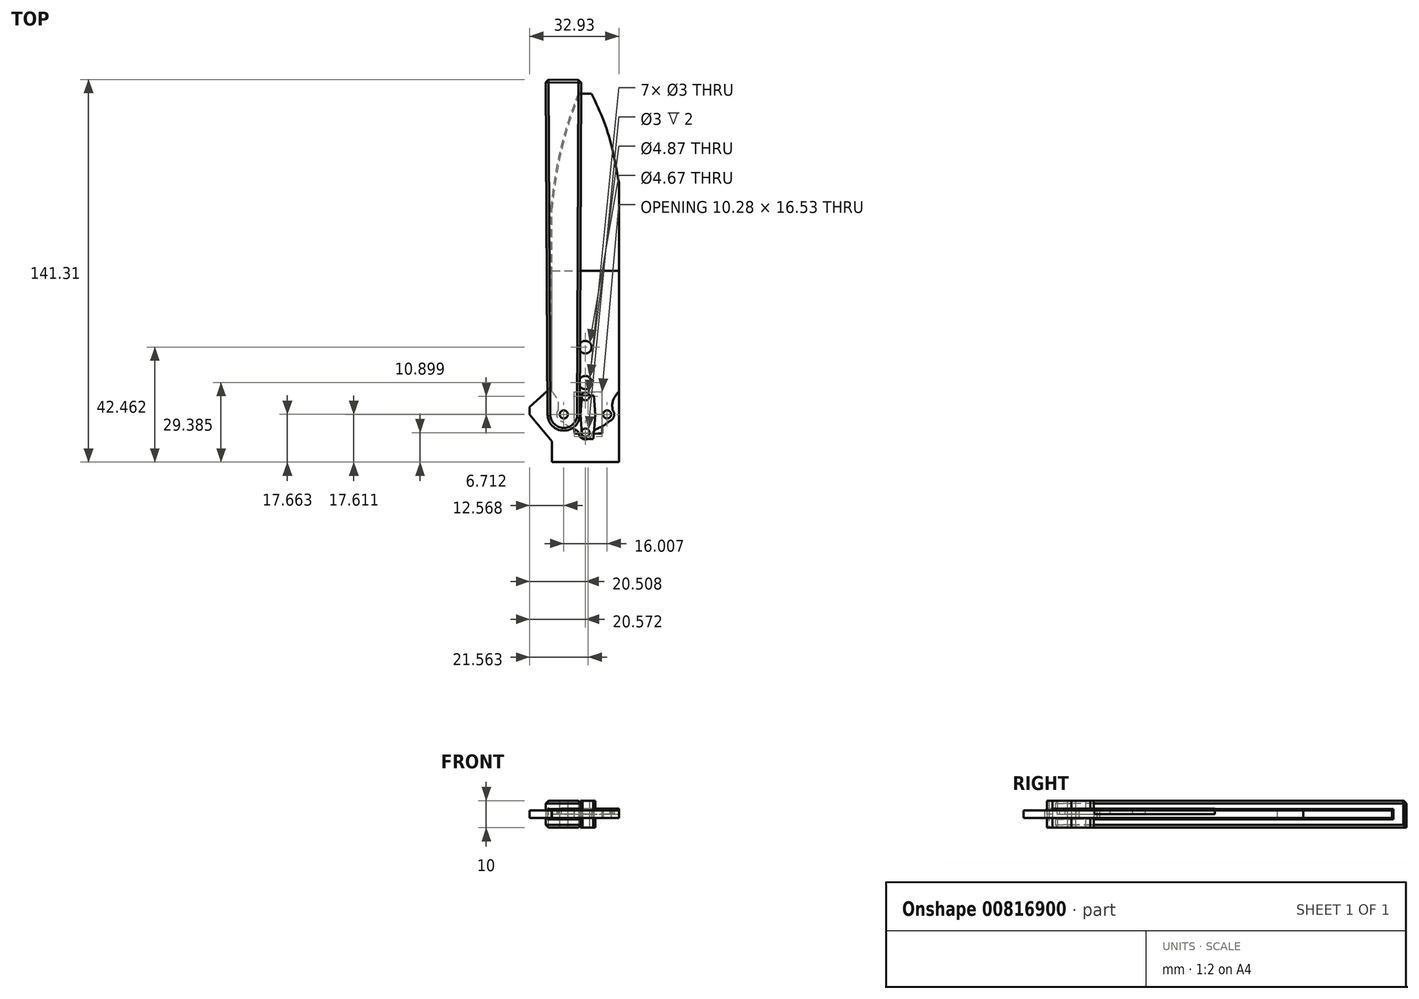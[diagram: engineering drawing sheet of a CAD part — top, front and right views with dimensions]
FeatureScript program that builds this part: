
annotation { "Feature Type Name" : "Feature", "Feature Type Description" : "" }
export const myFeature = defineFeature(function(context is Context, id is Id, definition is map)
    precondition{}
    {
        {
            var Q0;
            Q0=qCreatedBy(makeId("Top.planeOp"),FACE);
            var sketch = newSketch(context, id + "F0", { "sketchPlane" : qUnion([Q0])});
            skLineSegment(sketch, "E0.bottom", {"start": v(-13.28, -70.6) * mm, "end": v(11.44, -70.6) * mm});
            skLineSegment(sketch, "E0.top", {"start": v(-13.28, 65.4) * mm, "end": v(11.44, 65.4) * mm});
            skLineSegment(sketch, "E0.left", {"start": v(-13.28, -70.6) * mm, "end": v(-13.28, 22.93) * mm});
            skLineSegment(sketch, "E0.right", {"start": v(11.44, -70.6) * mm, "end": v(11.44, 32.61) * mm});
            skLineSegment(sketch, "E1", {"start": v(-0.92, 65.4) * mm, "end": v(-0.92, -70.6) * mm, "construction": true});
            skCircle(sketch, "E2", {"center": v(-0.92, -59.71) * mm, "radius": 1.5 * mm});
            skCircle(sketch, "E3", {"center": v(-0.92, -46.29) * mm, "radius": 1.5 * mm});
            skLineSegment(sketch, "E4", {"start": v(-13.28, -53) * mm, "end": v(-0.92, -53) * mm, "construction": true});
            skCircle(sketch, "E5", {"center": v(-8.92, -53) * mm, "radius": 1.5 * mm});
            skCircle(sketch, "E6.MirrorC", {"center": v(7.08, -53) * mm, "radius": 1.5 * mm});
            skFitSpline(sketch, "E7", {"points": [v(-3.02, 65.4) * mm, v(-6.8, 55.16) * mm, v(-11.04, 38.52) * mm, v(-13.28, 22.93) * mm], "startDerivative": vector(-13.1, -32.8) * mm, "endDerivative": vector(-5.15, -43.8) * mm});
            skFitSpline(sketch, "E8", {"points": [v(1.36, 65.4) * mm, v(7.27, 51.38) * mm, v(11.44, 32.61) * mm], "startDerivative": vector(13.66, -28.43) * mm, "endDerivative": vector(6.64, -36.96) * mm});
            skLineSegment(sketch, "E9", {"start": v(-13.28, -42.85) * mm, "end": v(-21.49, -50.18) * mm});
            skLineSegment(sketch, "E10", {"start": v(-21.49, -50.18) * mm, "end": v(-21.49, -53) * mm});
            skLineSegment(sketch, "E11", {"start": v(-21.49, -53) * mm, "end": v(-13.28, -62.88) * mm});
            skSolve(sketch);
        }
        {
            var Q0;
            Q0=makeQuery(id+"F0.imprint","IMPRINT",FACE,{"disambiguationData":[TD([[makeQuery(id+"F0.imprint","IMPRINT",EDGE,{"derivedFrom":sQuery(id+"F0.wireOp",EDGE,"E0.bottom")}),1.0]])]});
            var Q1;
            {var subQ0=sQuery(id+"F0.wireOp",EDGE,"E9");Q1=makeQuery(id+"F0.imprint","IMPRINT",FACE,{"disambiguationData":[TD([[makeQuery(id+"F0.imprint","IMPRINT",EDGE,{"derivedFrom":subQ0}),1.0]])]});}
            extrude(context, id + "F1", {"entities" : qUnion([Q0, Q1]), "endBound" : BoundingType.SYMMETRIC, "depth" : 2.75 * mm, "offsetDistance" : 25 * mm});
        }
        {
            var Q0;
            Q0=qCreatedBy(makeId("Top.planeOp"),FACE);
            var sketch = newSketch(context, id + "F2", { "sketchPlane" : qUnion([Q0])});
            skCircle(sketch, "E12.0", {"center": v(-8.92, -53) * mm, "radius": 1.5 * mm});
            skCircle(sketch, "E13.0", {"center": v(-0.92, -46.29) * mm, "radius": 1.5 * mm});
            skCircle(sketch, "E14.0", {"center": v(-0.92, -59.71) * mm, "radius": 1.5 * mm});
            skArc(sketch, "E15", {"start": v(-14.89, -53.03) * mm, "mid": v(-8.92, -58.97) * mm, "end": v(-2.95, -53.02) * mm});
            skLineSegment(sketch, "E16", {"start": v(-2.54, 70.47) * mm, "end": v(-15.54, 70.72) * mm});
            skLineSegment(sketch, "E17", {"start": v(-15.54, 70.72) * mm, "end": v(-14.89, -53.03) * mm});
            skLineSegment(sketch, "E18", {"start": v(-2.54, 70.47) * mm, "end": v(-2.95, -53.02) * mm});
            skPoint(sketch, "E19.centerSnap0", {"position": v(-9.04, 70.6) * mm});
            skSolve(sketch);
        }
        {
            var Q0;
            Q0 = qSketchRegion(id + "F2", true);
            extrude(context, id + "F3", {"entities" : qUnion([Q0]), "endBound" : BoundingType.SYMMETRIC, "depth" : 10 * mm, "offsetDistance" : 25 * mm});
        }
        {
            var Q0;
            Q0=makeQuery(id+"F1.opExtrude","SWEPT_BODY",BODY,{"disambiguationData":[OSD([sQuery(id+"F0.wireOp",EDGE,"E0.bottom"),sQuery(id+"F0.wireOp",EDGE,"E0.top"),sQuery(id+"F0.wireOp",EDGE,"E0.left"),sQuery(id+"F0.wireOp",EDGE,"E0.right"),sQuery(id+"F0.wireOp",EDGE,"E2"),sQuery(id+"F0.wireOp",EDGE,"E3"),sQuery(id+"F0.wireOp",EDGE,"E5"),sQuery(id+"F0.wireOp",EDGE,"E6.MirrorC")])]});
            var Q1;
            Q1=makeQuery(id+"F3.opExtrude","SWEPT_BODY",BODY,{"disambiguationData":[OSD([sQuery(id+"F2.wireOp",EDGE,"E12.0"),sQuery(id+"F2.wireOp",EDGE,"E15"),sQuery(id+"F2.wireOp",EDGE,"E16"),sQuery(id+"F2.wireOp",EDGE,"E17"),sQuery(id+"F2.wireOp",EDGE,"E18"),sQuery(id+"F2.wireOp",EDGE,"E19"),sQuery(id+"F2.wireOp",EDGE,"EcuJtlNR-yBzJ-jaTy-znSZ-DWJmyuvK7YeQ"),sQuery(id+"F2.wireOp",EDGE,"04znlC2m-Oqa3-mzNC-y53b-a8wuwB7Aq2dO")])]});
            booleanBodies(context, id + "F4", {"operationType" : BooleanOperationType.SUBTRACTION, "tools" : qUnion([Q0]), "targets" : qUnion([Q1]), "offset" : true, "offsetAll" : true, "offsetDistance" : 0.5 * mm, "keepTools" : true});
        }
        {
            var Q0;
            Q0=makeQuery(id+"F3.opExtrude","CAP_EDGE",EDGE,{"disambiguationData":[OSD([sQuery(id+"F2.wireOp",EDGE,"E16")])],"isStart":false});
            var Q1;
            Q1=makeQuery(id+"F3.opExtrude","CAP_EDGE",EDGE,{"disambiguationData":[OSD([sQuery(id+"F2.wireOp",EDGE,"E18")])],"isStart":false});
            var Q2;
            Q2=makeQuery(id+"F3.opExtrude","CAP_EDGE",EDGE,{"disambiguationData":[OSD([sQuery(id+"F2.wireOp",EDGE,"E19")])],"isStart":false});
            var Q3;
            Q3=makeQuery(id+"F3.opExtrude","CAP_EDGE",EDGE,{"disambiguationData":[OSD([sQuery(id+"F2.wireOp",EDGE,"EcuJtlNR-yBzJ-jaTy-znSZ-DWJmyuvK7YeQ")])],"isStart":false});
            var Q4;
            Q4=makeQuery(id+"F3.opExtrude","CAP_EDGE",EDGE,{"disambiguationData":[OSD([sQuery(id+"F2.wireOp",EDGE,"04znlC2m-Oqa3-mzNC-y53b-a8wuwB7Aq2dO")])],"isStart":false});
            var Q5;
            Q5=makeQuery(id+"F3.opExtrude","CAP_EDGE",EDGE,{"disambiguationData":[OSD([sQuery(id+"F2.wireOp",EDGE,"E18")])],"isStart":true});
            var Q6;
            Q6=makeQuery(id+"F3.opExtrude","CAP_EDGE",EDGE,{"disambiguationData":[OSD([sQuery(id+"F2.wireOp",EDGE,"04znlC2m-Oqa3-mzNC-y53b-a8wuwB7Aq2dO")])],"isStart":true});
            var Q7;
            Q7=makeQuery(id+"F3.opExtrude","CAP_EDGE",EDGE,{"disambiguationData":[OSD([sQuery(id+"F2.wireOp",EDGE,"EcuJtlNR-yBzJ-jaTy-znSZ-DWJmyuvK7YeQ")])],"isStart":true});
            var Q8;
            Q8=makeQuery(id+"F3.opExtrude","CAP_EDGE",EDGE,{"disambiguationData":[OSD([sQuery(id+"F2.wireOp",EDGE,"E19")])],"isStart":true});
            var Q9;
            Q9=makeQuery(id+"F3.opExtrude","SWEPT_EDGE",EDGE,{"disambiguationData":[OSD([sQuery(id+"F2.wireOp",EDGE,"E16"),sQuery(id+"F2.wireOp",EDGE,"E17")])]});
            var Q10;
            Q10=makeQuery(id+"F3.opExtrude","SWEPT_EDGE",EDGE,{"disambiguationData":[OSD([sQuery(id+"F2.wireOp",EDGE,"E16"),sQuery(id+"F2.wireOp",EDGE,"E18")])]});
            chamfer(context, id + "F5", {"entities" : qUnion([Q0, Q1, Q2, Q3, Q4, Q5, Q6, Q7, Q8, Q9, Q10]), "width" : 1 * mm, "tangentPropagation" : true});
        }
        {
            var Q0;
            Q0=qCreatedBy(makeId("Top.planeOp"),FACE);
            var sketch = newSketch(context, id + "F6", { "sketchPlane" : qUnion([Q0])});
            skCircle(sketch, "E20.0", {"center": v(-0.92, -59.71) * mm, "radius": 1.5 * mm});
            skCircle(sketch, "E21.0", {"center": v(-0.92, -46.29) * mm, "radius": 1.5 * mm});
            skCircle(sketch, "E22.0", {"center": v(-8.92, -53) * mm, "radius": 1.5 * mm});
            skCircle(sketch, "E23.0", {"center": v(7.08, -53) * mm, "radius": 1.5 * mm});
            skArc(sketch, "E24", {"start": v(-3.4, -59.87) * mm, "mid": v(-0.92, -62.2) * mm, "end": v(1.56, -59.87) * mm});
            skArc(sketch, "E25", {"start": v(8, -55.45) * mm, "mid": v(9.61, -53.68) * mm, "end": v(9.11, -51.34) * mm});
            skArc(sketch, "E26", {"start": v(-10.95, -51.34) * mm, "mid": v(-11.45, -53.68) * mm, "end": v(-9.84, -55.45) * mm});
            skFitSpline(sketch, "E27", {"points": [v(1.56, -59.87) * mm, v(5.77, -57.1) * mm, v(8, -55.45) * mm], "startDerivative": vector(1.74, 6.3) * mm, "endDerivative": vector(5.16, 2.88) * mm});
            skFitSpline(sketch, "E28.MirrorCS", {"points": [v(-3.4, -59.87) * mm, v(-7.61, -57.1) * mm, v(-9.84, -55.45) * mm], "startDerivative": vector(-1.74, 6.3) * mm, "endDerivative": vector(-5.16, 2.88) * mm});
            skFitSpline(sketch, "E29", {"points": [v(-10.95, -51.34) * mm, v(-11.03, -48.05) * mm, v(-13.28, -44.48) * mm], "startDerivative": vector(0.78, 7.08) * mm, "endDerivative": vector(-5.3, 6.65) * mm});
            skFitSpline(sketch, "E30.MirrorCS", {"points": [v(9.11, -51.34) * mm, v(9.2, -48.05) * mm, v(11.44, -44.48) * mm], "startDerivative": vector(-0.78, 7.08) * mm, "endDerivative": vector(5.3, 6.65) * mm});
            skPoint(sketch, "E31.0.2.end.orphan", {"position": v(11.44, -70.6) * mm});
            skPoint(sketch, "E32.orphan", {"position": v(-13.28, -70.6) * mm});
            skPoint(sketch, "E31.0.0.end.orphan", {"position": v(-3.02, 65.4) * mm});
            skPoint(sketch, "E31.0.0.start.orphan", {"position": v(1.36, 65.4) * mm});
            skCircle(sketch, "E33", {"center": v(-0.98, -41.23) * mm, "radius": 2.44 * mm});
            skCircle(sketch, "E34", {"center": v(-0.98, -28.15) * mm, "radius": 2.34 * mm});
            skLineSegment(sketch, "E35", {"start": v(-13.28, -44.48) * mm, "end": v(-13.28, 0) * mm});
            skLineSegment(sketch, "E36", {"start": v(-13.28, 0) * mm, "end": v(11.44, 0) * mm});
            skLineSegment(sketch, "E37", {"start": v(11.44, 0) * mm, "end": v(11.44, -44.48) * mm});
            skSolve(sketch);
        }
        {
            var Q0;
            Q0 = qSketchRegion(id + "F6", true);
            extrude(context, id + "F7", {"entities" : qUnion([Q0]), "depth" : 2 * mm, "offsetDistance" : 25 * mm});
        }
        {
            var Q0;
            Q0=qCreatedBy(makeId("Top.planeOp"),FACE);
            var sketch = newSketch(context, id + "F8", { "sketchPlane" : qUnion([Q0])});
            skLineSegment(sketch, "E38", {"start": v(-2.25, -60.02) * mm, "end": v(-2.75, -53.03) * mm});
            skLineSegment(sketch, "E39.MirrorCS", {"start": v(2.25, -60.02) * mm, "end": v(2.75, -53.03) * mm});
            skLineSegment(sketch, "E40", {"start": v(-2.25, -60.02) * mm, "end": v(2.25, -60.02) * mm, "construction": true});
            skLineSegment(sketch, "E41", {"start": v(-2.75, -53.03) * mm, "end": v(2.75, -53.03) * mm, "construction": true});
            skLineSegment(sketch, "E42.MirrorCS", {"start": v(2.25, -46.05) * mm, "end": v(2.75, -53.03) * mm});
            skLineSegment(sketch, "E43.MirrorCS", {"start": v(-2.25, -46.05) * mm, "end": v(2.25, -46.05) * mm});
            skLineSegment(sketch, "E44.MirrorCS", {"start": v(-2.25, -46.05) * mm, "end": v(-2.75, -53.03) * mm});
            skLineSegment(sketch, "E45", {"start": v(-2.25, -60.02) * mm, "end": v(-1.92, -62.03) * mm});
            skLineSegment(sketch, "E46.MirrorCS", {"start": v(2.25, -60.02) * mm, "end": v(1.92, -62.03) * mm});
            skLineSegment(sketch, "E47", {"start": v(-1.92, -62.03) * mm, "end": v(1.92, -62.03) * mm});
            skLineSegment(sketch, "E48.bottom", {"start": v(-5.07, -60.02) * mm, "end": v(5.21, -60.02) * mm});
            skLineSegment(sketch, "E48.top", {"start": v(-5.07, -44.68) * mm, "end": v(5.21, -44.68) * mm});
            skLineSegment(sketch, "E48.left", {"start": v(-5.07, -60.02) * mm, "end": v(-5.07, -44.68) * mm});
            skLineSegment(sketch, "E48.right", {"start": v(5.21, -60.02) * mm, "end": v(5.21, -44.68) * mm});
            skSolve(sketch);
        }
        {
            var Q0;
            {var subQ1=sQuery(id+"F8.wireOp",EDGE,"E38");Q0=makeQuery(id+"F8.imprint","IMPRINT",FACE,{"disambiguationData":[TD([[makeQuery(id+"F8.imprint","IMPRINT",EDGE,{"derivedFrom":subQ1}),-1.0]])]});}
            var Q1;
            {var subQ0=sQuery(id+"F8.wireOp",EDGE,"E45");Q1=makeQuery(id+"F8.imprint","IMPRINT",FACE,{"disambiguationData":[TD([[makeQuery(id+"F8.imprint","IMPRINT",EDGE,{"derivedFrom":subQ0}),1.0]])]});}
            extrude(context, id + "F9", {"entities" : qUnion([Q0, Q1]), "endBound" : BoundingType.SYMMETRIC, "depth" : 10 * mm, "offsetDistance" : 25 * mm});
        }
        {
            var Q0;
            {var subQ1=sQuery(id+"F8.wireOp",EDGE,"E38");Q0=makeQuery(id+"F8.imprint","IMPRINT",FACE,{"disambiguationData":[TD([[makeQuery(id+"F8.imprint","IMPRINT",EDGE,{"derivedFrom":subQ1}),-1.0]])]});}
            var Q1;
            {var subQ3=sQuery(id+"F8.wireOp",EDGE,"E38");Q1=makeQuery(id+"F8.imprint","IMPRINT",FACE,{"disambiguationData":[TD([[makeQuery(id+"F8.imprint","IMPRINT",EDGE,{"derivedFrom":subQ3}),1.0]])]});}
            extrude(context, id + "F10", {"entities" : qUnion([Q0, Q1]), "operationType" : NewBodyOperationType.REMOVE, "endBound" : BoundingType.SYMMETRIC, "oppositeDirection" : true, "depth" : 2.8 * mm, "offsetDistance" : 25 * mm});
        }
    });
